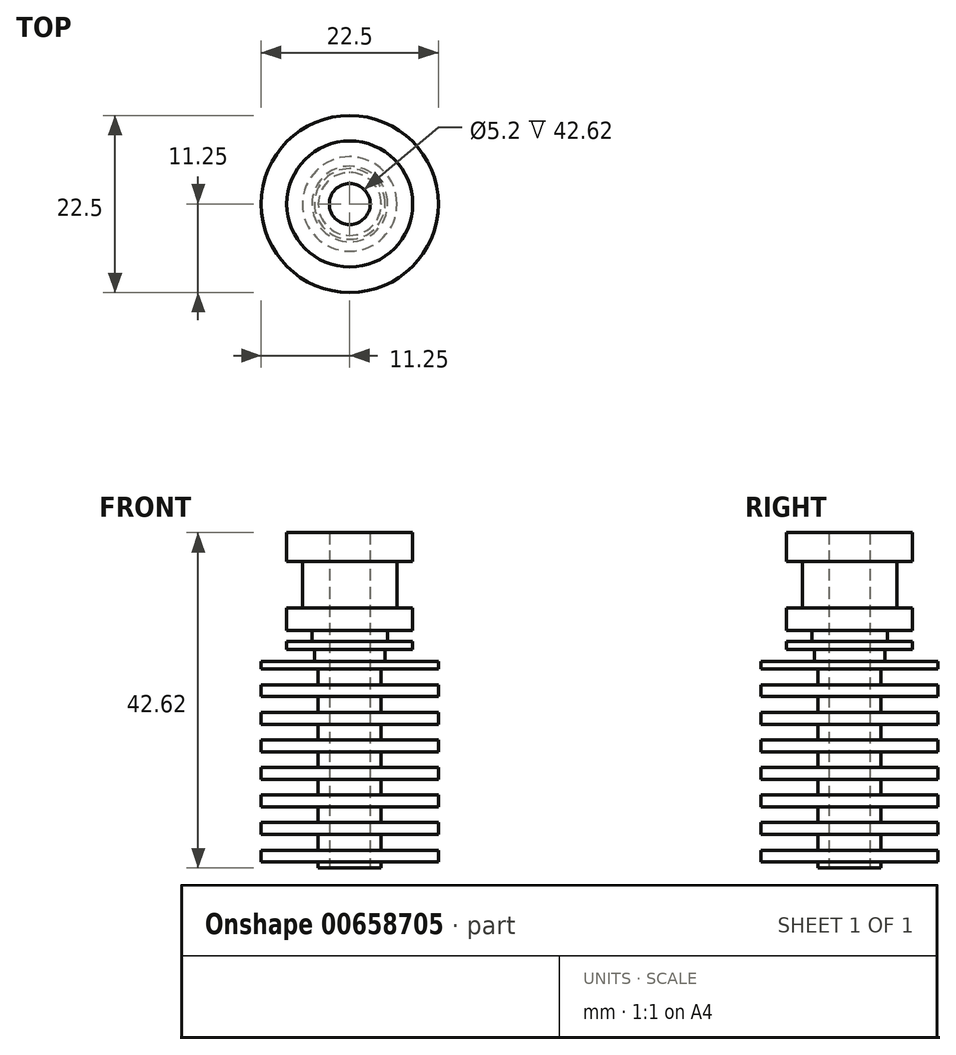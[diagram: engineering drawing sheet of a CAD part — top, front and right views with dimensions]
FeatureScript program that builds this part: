
annotation { "Feature Type Name" : "Feature", "Feature Type Description" : "" }
export const myFeature = defineFeature(function(context is Context, id is Id, definition is map)
    precondition{}
    {
        {
            var Q0;
            Q0=qCreatedBy(makeId("Front.planeOp"),FACE);
            var sketch = newSketch(context, id + "F0", { "sketchPlane" : qUnion([Q0])});
            skLineSegment(sketch, "E0", {"start": v(2.6, 0) * mm, "end": v(2.6, 42.62) * mm});
            skLineSegment(sketch, "E1", {"start": v(2.6, 42.62) * mm, "end": v(8, 42.62) * mm});
            skLineSegment(sketch, "E2", {"start": v(8, 42.62) * mm, "end": v(8, 38.97) * mm});
            skLineSegment(sketch, "E3", {"start": v(8, 38.97) * mm, "end": v(6, 38.97) * mm});
            skLineSegment(sketch, "E4", {"start": v(6, 38.97) * mm, "end": v(6, 33.07) * mm});
            skLineSegment(sketch, "E5", {"start": v(6, 33.07) * mm, "end": v(8, 33.07) * mm});
            skLineSegment(sketch, "E6", {"start": v(8, 33.07) * mm, "end": v(8, 30.2) * mm});
            skLineSegment(sketch, "E7", {"start": v(8, 30.2) * mm, "end": v(4.8, 30.2) * mm});
            skLineSegment(sketch, "E8", {"start": v(4.8, 30.2) * mm, "end": v(4.8, 28.77) * mm});
            skLineSegment(sketch, "E9", {"start": v(4.8, 28.77) * mm, "end": v(8, 28.77) * mm});
            skLineSegment(sketch, "E10", {"start": v(8, 28.77) * mm, "end": v(8, 27.77) * mm});
            skLineSegment(sketch, "E11", {"start": v(8, 27.77) * mm, "end": v(4.48, 27.77) * mm});
            skLineSegment(sketch, "E12", {"start": v(4.48, 27.77) * mm, "end": v(4.48, 26.28) * mm});
            skLineSegment(sketch, "E13", {"start": v(4.48, 26.28) * mm, "end": v(11.25, 26.28) * mm});
            skLineSegment(sketch, "E14", {"start": v(11.25, 26.28) * mm, "end": v(11.25, 0) * mm});
            skLineSegment(sketch, "E15", {"start": v(11.25, 0) * mm, "end": v(2.6, 0) * mm});
            skLineSegment(sketch, "E16", {"start": v(0, 0) * mm, "end": v(0, 10.9) * mm});
            skSolve(sketch);
        }
        {
            var Q0;
            Q0=makeQuery(id+"F0.imprint","IMPRINT",FACE,{"disambiguationData":[TD([[makeQuery(id+"F0.imprint","IMPRINT",EDGE,{"derivedFrom":sQuery(id+"F0.wireOp",EDGE,"E0")}),-1.0]])]});
            var Q1;
            Q1=sQuery(id+"F0.wireOp",EDGE,"E16");
            revolve(context, id + "F1", {"entities" : qUnion([Q0]), "axis" : qUnion([Q1]), "revolveType" : RevolveType.FULL});
        }
        {
            var Q0;
            Q0=qCreatedBy(makeId("Front.planeOp"),FACE);
            var sketch = newSketch(context, id + "F2", { "sketchPlane" : qUnion([Q0])});
            skLineSegment(sketch, "E17.bottom", {"start": v(15.21, 25.28) * mm, "end": v(4, 25.28) * mm});
            skLineSegment(sketch, "E17.top", {"start": v(15.21, 23.28) * mm, "end": v(4, 23.28) * mm});
            skLineSegment(sketch, "E17.left", {"start": v(15.21, 25.28) * mm, "end": v(15.21, 23.28) * mm});
            skLineSegment(sketch, "E17.right", {"start": v(4, 25.28) * mm, "end": v(4, 23.28) * mm});
            skLineSegment(sketch, "E18.0.1.0", {"start": v(15.21, 21.78) * mm, "end": v(15.21, 19.78) * mm});
            skLineSegment(sketch, "E18.0.1.1", {"start": v(15.21, 21.78) * mm, "end": v(4, 21.78) * mm});
            skLineSegment(sketch, "E18.0.1.2", {"start": v(15.21, 19.78) * mm, "end": v(4, 19.78) * mm});
            skLineSegment(sketch, "E18.0.1.3", {"start": v(4, 21.78) * mm, "end": v(4, 19.78) * mm});
            skLineSegment(sketch, "E18.0.2.0", {"start": v(15.21, 18.28) * mm, "end": v(15.21, 16.28) * mm});
            skLineSegment(sketch, "E18.0.2.1", {"start": v(15.21, 18.28) * mm, "end": v(4, 18.28) * mm});
            skLineSegment(sketch, "E18.0.2.2", {"start": v(15.21, 16.28) * mm, "end": v(4, 16.28) * mm});
            skLineSegment(sketch, "E18.0.2.3", {"start": v(4, 18.28) * mm, "end": v(4, 16.28) * mm});
            skLineSegment(sketch, "E18.0.3.0", {"start": v(15.21, 14.78) * mm, "end": v(15.21, 12.78) * mm});
            skLineSegment(sketch, "E18.0.3.1", {"start": v(15.21, 14.78) * mm, "end": v(4, 14.78) * mm});
            skLineSegment(sketch, "E18.0.3.2", {"start": v(15.21, 12.78) * mm, "end": v(4, 12.78) * mm});
            skLineSegment(sketch, "E18.0.3.3", {"start": v(4, 14.78) * mm, "end": v(4, 12.78) * mm});
            skLineSegment(sketch, "E18.0.4.0", {"start": v(15.21, 11.28) * mm, "end": v(15.21, 9.28) * mm});
            skLineSegment(sketch, "E18.0.4.1", {"start": v(15.21, 11.28) * mm, "end": v(4, 11.28) * mm});
            skLineSegment(sketch, "E18.0.4.2", {"start": v(15.21, 9.28) * mm, "end": v(4, 9.28) * mm});
            skLineSegment(sketch, "E18.0.4.3", {"start": v(4, 11.28) * mm, "end": v(4, 9.28) * mm});
            skLineSegment(sketch, "E18.0.5.0", {"start": v(15.21, 7.78) * mm, "end": v(15.21, 5.78) * mm});
            skLineSegment(sketch, "E18.0.5.1", {"start": v(15.21, 7.78) * mm, "end": v(4, 7.78) * mm});
            skLineSegment(sketch, "E18.0.5.2", {"start": v(15.21, 5.78) * mm, "end": v(4, 5.78) * mm});
            skLineSegment(sketch, "E18.0.5.3", {"start": v(4, 7.78) * mm, "end": v(4, 5.78) * mm});
            skLineSegment(sketch, "E18.0.6.0", {"start": v(15.21, 4.28) * mm, "end": v(15.21, 2.28) * mm});
            skLineSegment(sketch, "E18.0.6.1", {"start": v(15.21, 4.28) * mm, "end": v(4, 4.28) * mm});
            skLineSegment(sketch, "E18.0.6.2", {"start": v(15.21, 2.28) * mm, "end": v(4, 2.28) * mm});
            skLineSegment(sketch, "E18.0.6.3", {"start": v(4, 4.28) * mm, "end": v(4, 2.28) * mm});
            skLineSegment(sketch, "E18.0.7.0", {"start": v(15.21, 0.78) * mm, "end": v(15.21, -1.22) * mm});
            skLineSegment(sketch, "E18.0.7.1", {"start": v(15.21, 0.78) * mm, "end": v(4, 0.78) * mm});
            skLineSegment(sketch, "E18.0.7.2", {"start": v(15.21, -1.22) * mm, "end": v(4, -1.22) * mm});
            skLineSegment(sketch, "E18.0.7.3", {"start": v(4, 0.78) * mm, "end": v(4, -1.22) * mm});
            skLineSegment(sketch, "E18.0.8.0", {"start": v(15.21, -2.72) * mm, "end": v(15.21, -4.72) * mm});
            skLineSegment(sketch, "E18.0.8.1", {"start": v(15.21, -2.72) * mm, "end": v(4, -2.72) * mm});
            skLineSegment(sketch, "E18.0.8.2", {"start": v(15.21, -4.72) * mm, "end": v(4, -4.72) * mm});
            skLineSegment(sketch, "E18.0.8.3", {"start": v(4, -2.72) * mm, "end": v(4, -4.72) * mm});
            skLineSegment(sketch, "E18.direction1", {"start": v(15.21, 23.28) * mm, "end": v(40.21, 23.28) * mm, "construction": true});
            skLineSegment(sketch, "E18.direction2", {"start": v(15.21, 23.28) * mm, "end": v(15.21, 19.78) * mm, "construction": true});
            skLineSegment(sketch, "E19", {"start": v(0, 0) * mm, "end": v(0, 6.66) * mm});
            skSolve(sketch);
        }
        {
            var Q0;
            Q0=makeQuery(id+"F2.imprint","IMPRINT",FACE,{"disambiguationData":[TD([[makeQuery(id+"F2.imprint","IMPRINT",EDGE,{"derivedFrom":sQuery(id+"F2.wireOp",EDGE,"E18.0.8.0")}),-1.0]])]});
            var Q1;
            Q1=makeQuery(id+"F2.imprint","IMPRINT",FACE,{"disambiguationData":[TD([[makeQuery(id+"F2.imprint","IMPRINT",EDGE,{"derivedFrom":sQuery(id+"F2.wireOp",EDGE,"E18.0.7.0")}),-1.0]])]});
            var Q2;
            Q2=makeQuery(id+"F2.imprint","IMPRINT",FACE,{"disambiguationData":[TD([[makeQuery(id+"F2.imprint","IMPRINT",EDGE,{"derivedFrom":sQuery(id+"F2.wireOp",EDGE,"E18.0.6.0")}),-1.0]])]});
            var Q3;
            Q3=makeQuery(id+"F2.imprint","IMPRINT",FACE,{"disambiguationData":[TD([[makeQuery(id+"F2.imprint","IMPRINT",EDGE,{"derivedFrom":sQuery(id+"F2.wireOp",EDGE,"E18.0.5.0")}),-1.0]])]});
            var Q4;
            Q4=makeQuery(id+"F2.imprint","IMPRINT",FACE,{"disambiguationData":[TD([[makeQuery(id+"F2.imprint","IMPRINT",EDGE,{"derivedFrom":sQuery(id+"F2.wireOp",EDGE,"E18.0.4.0")}),-1.0]])]});
            var Q5;
            Q5=makeQuery(id+"F2.imprint","IMPRINT",FACE,{"disambiguationData":[TD([[makeQuery(id+"F2.imprint","IMPRINT",EDGE,{"derivedFrom":sQuery(id+"F2.wireOp",EDGE,"E18.0.3.0")}),-1.0]])]});
            var Q6;
            Q6=makeQuery(id+"F2.imprint","IMPRINT",FACE,{"disambiguationData":[TD([[makeQuery(id+"F2.imprint","IMPRINT",EDGE,{"derivedFrom":sQuery(id+"F2.wireOp",EDGE,"E18.0.2.0")}),-1.0]])]});
            var Q7;
            Q7=makeQuery(id+"F2.imprint","IMPRINT",FACE,{"disambiguationData":[TD([[makeQuery(id+"F2.imprint","IMPRINT",EDGE,{"derivedFrom":sQuery(id+"F2.wireOp",EDGE,"E18.0.1.0")}),-1.0]])]});
            var Q8;
            Q8=makeQuery(id+"F2.imprint","IMPRINT",FACE,{"disambiguationData":[TD([[makeQuery(id+"F2.imprint","IMPRINT",EDGE,{"derivedFrom":sQuery(id+"F2.wireOp",EDGE,"E17.bottom")}),1.0]])]});
            var Q9;
            Q9=sQuery(id+"F2.wireOp",EDGE,"E19");
            revolve(context, id + "F3", {"operationType" : NewBodyOperationType.REMOVE, "entities" : qUnion([Q0, Q1, Q2, Q3, Q4, Q5, Q6, Q7, Q8]), "axis" : qUnion([Q9]), "revolveType" : RevolveType.FULL, "oppositeDirection" : true});
        }
    });
